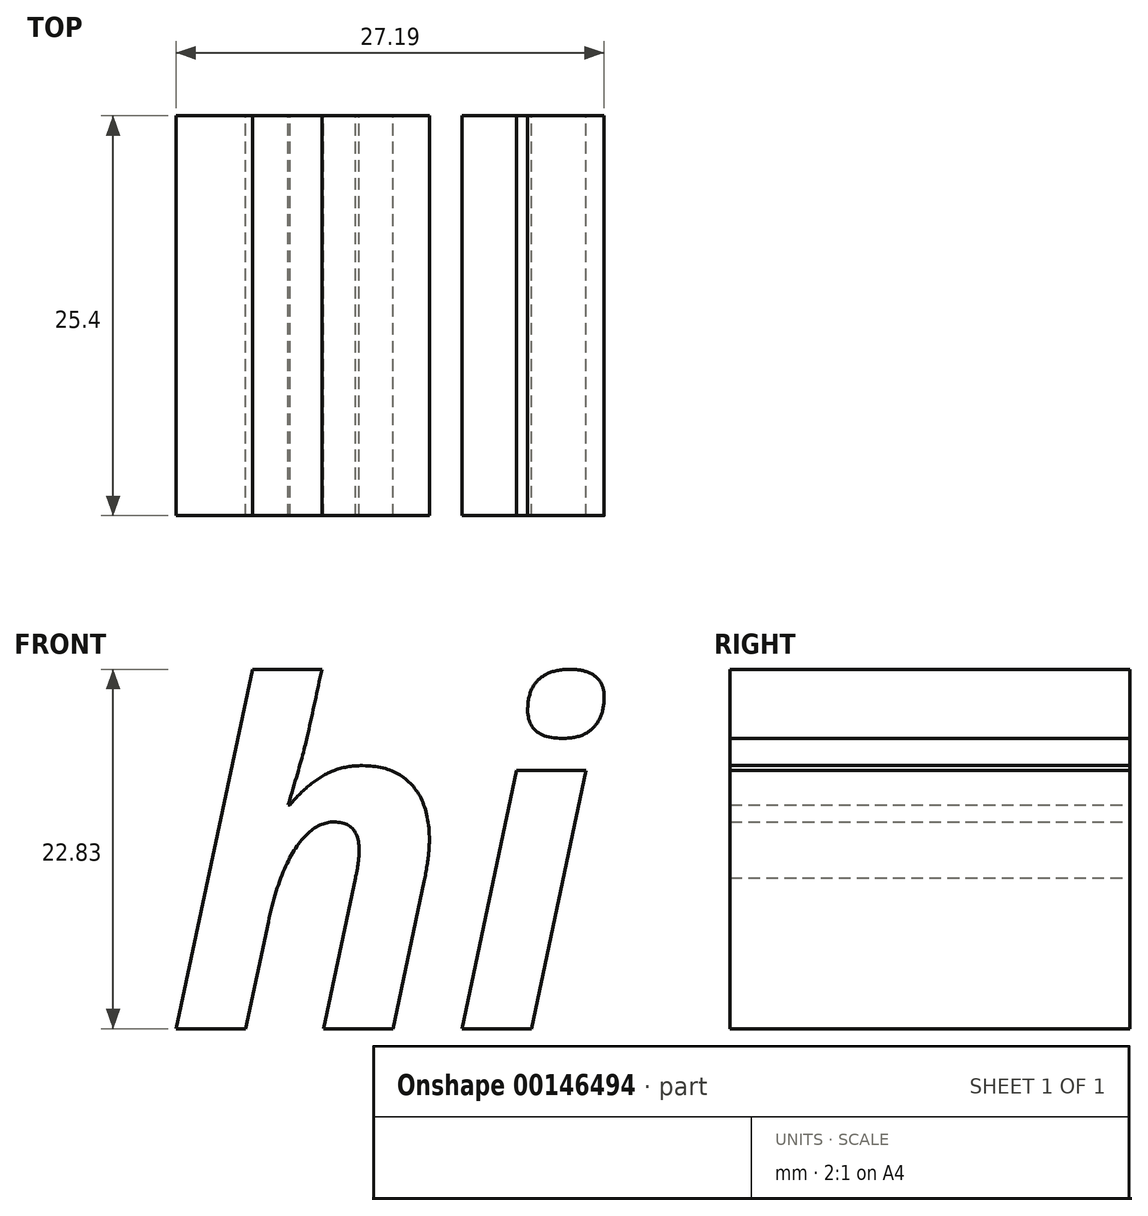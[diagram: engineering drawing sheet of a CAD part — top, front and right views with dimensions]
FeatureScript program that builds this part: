
annotation { "Feature Type Name" : "Feature", "Feature Type Description" : "" }
export const myFeature = defineFeature(function(context is Context, id is Id, definition is map)
    precondition{}
    {
        {
            var Q0;
            Q0=qCreatedBy(makeId("Front.planeOp"),FACE);
            var sketch = newSketch(context, id + "F0", { "sketchPlane" : qUnion([Q0])});
            skText(sketch, "E0", { "text": "hi\n", "fontName": "OpenSans-BoldItalic.ttf"});
            skPoint(sketch, "E1", {"position": v(-20.8, 34.84) * mm});
            skCircle(sketch, "E2", {"center": v(-20.8, 34.84) * mm, "radius": 18.36 * mm});
            const initialGuessF0  = {"E0": [-0.03563, 0.02402, 1, 0, 0.02163]};
            skSetInitialGuess(sketch, initialGuessF0);
            skSolve(sketch);
        }
        {
            var Q0;
            Q0=makeQuery(id+"F0.imprint","IMPRINT",FACE,{"disambiguationData":[TD([[makeQuery(id+"F0.imprint","IMPRINT",EDGE,{"derivedFrom":sQuery(id+"F0.wireOp",EDGE,"E0.sketch_text.stroke-0")}),-1.0]])]});
            var Q1;
            Q1=makeQuery(id+"F0.imprint","IMPRINT",FACE,{"disambiguationData":[TD([[makeQuery(id+"F0.imprint","IMPRINT",EDGE,{"derivedFrom":sQuery(id+"F0.wireOp",EDGE,"E0.sketch_text.stroke-26")}),-1.0]])]});
            var Q2;
            Q2=makeQuery(id+"F0.imprint","IMPRINT",FACE,{"disambiguationData":[TD([[makeQuery(id+"F0.imprint","IMPRINT",EDGE,{"derivedFrom":sQuery(id+"F0.wireOp",EDGE,"E0.sketch_text.stroke-19")}),-1.0]])]});
            extrude(context, id + "F1", {"entities" : qUnion([Q0, Q1, Q2]), "depth" : 25.4 * mm});
        }
    });
